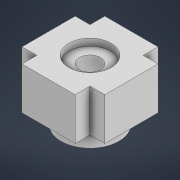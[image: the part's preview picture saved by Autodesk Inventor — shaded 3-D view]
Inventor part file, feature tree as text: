
AUTODESK INVENTOR PART (.ipt)
format: ipt  version: 2021 (Build 250183000, 183)  size: 313,344 bytes
history: native  units: mm
features: extrude x5, sketch x4, plane x1
ambient origin geometry x8: Origin, YZ Plane, XZ Plane, XY Plane, X Axis, Y Axis, Z Axis, Center Point
bodies: Volumenkörper1 (feature_tree)
feature tree (10):
  extrude  "Extrusion1"  Depth=11.75mm
  sketch  "Skizze2"  dims[d3=11.75mm d12=6.0mm d13=0.0mm]
  plane  "Arbeitsebene1"
  extrude  "Extrusion4"  Depth=6.0mm TaperAngle=0.0deg
  extrude  "Extrusion5"  Depth=6.0mm
  extrude  "Extrusion6"  Depth=2.5mm TaperAngle=0.0deg
  extrude  "Extrusion7"  Depth=2.1mm
  sketch  "Skizze1"  dims[d1=7.0mm d2=11.75mm]
  sketch  "Skizze5"  dims[d14=6.0mm d20=5.7mm]
  sketch  "Skizze6"  dims[d21=8.2mm d22=2.5mm d23=0.0mm d24=2.1mm d25=2.1mm d26=2.1mm d27=2.1mm d28=2.1mm d29=2.1mm d30=2.1mm d31=2.1mm d32=6.0mm d33=0.0mm d34=1.0mm d35=0.0mm d38=3.0mm d39=10.0mm d40=0.0mm d15=0.5mm d16=0.872665mm d17=0.5mm d18=0.872665mm d36=0.5mm d37=0.872665mm]
